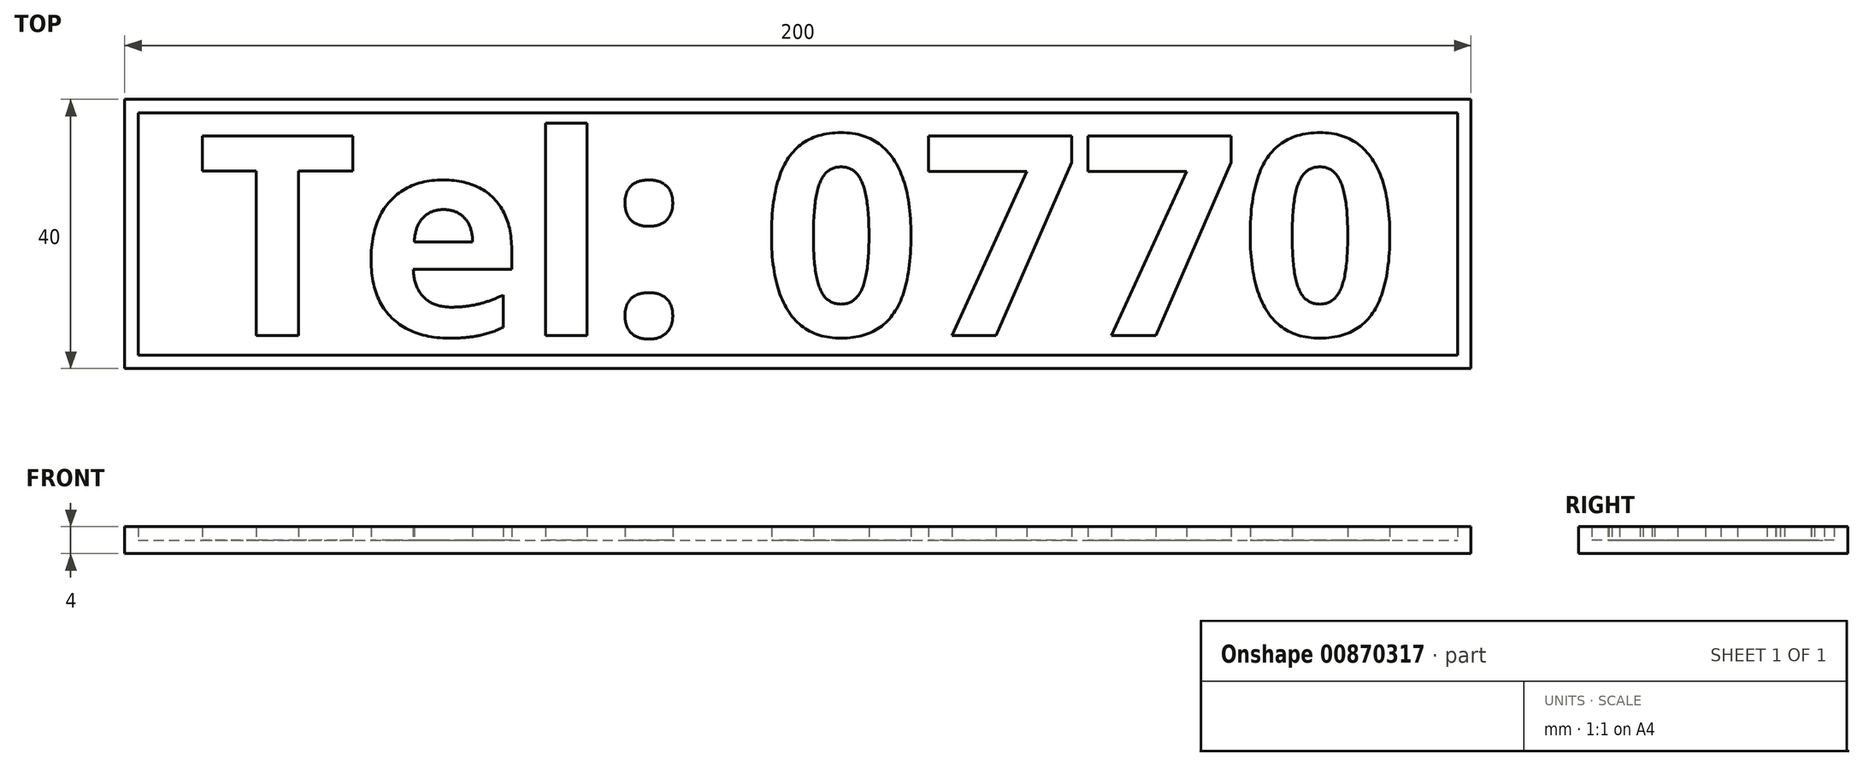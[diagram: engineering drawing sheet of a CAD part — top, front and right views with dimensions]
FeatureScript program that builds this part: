
annotation { "Feature Type Name" : "Feature", "Feature Type Description" : "" }
export const myFeature = defineFeature(function(context is Context, id is Id, definition is map)
    precondition{}
    {
        {
            var Q0;
            Q0=qCreatedBy(makeId("Top.planeOp"),FACE);
            var sketch = newSketch(context, id + "F0", { "sketchPlane" : qUnion([Q0])});
            skLineSegment(sketch, "E0.bottom", {"start": v(-100, 20) * mm, "end": v(100, 20) * mm});
            skLineSegment(sketch, "E0.top", {"start": v(-100, -20) * mm, "end": v(100, -20) * mm});
            skLineSegment(sketch, "E0.left", {"start": v(-100, 20) * mm, "end": v(-100, -20) * mm});
            skLineSegment(sketch, "E0.right", {"start": v(100, 20) * mm, "end": v(100, -20) * mm});
            skPoint(sketch, "E0.middle", {"position": v(0, 0) * mm});
            skLineSegment(sketch, "E1.bottom", {"start": v(-98, 18) * mm, "end": v(98, 18) * mm});
            skLineSegment(sketch, "E1.top", {"start": v(-98, -18) * mm, "end": v(98, -18) * mm});
            skLineSegment(sketch, "E1.left", {"start": v(-98, 18) * mm, "end": v(-98, -18) * mm});
            skLineSegment(sketch, "E1.right", {"start": v(98, 18) * mm, "end": v(98, -18) * mm});
            skSolve(sketch);
        }
        {
            var Q0;
            Q0=makeQuery(id+"F0.imprint","IMPRINT",FACE,{"disambiguationData":[TD([[makeQuery(id+"F0.imprint","IMPRINT",EDGE,{"derivedFrom":sQuery(id+"F0.wireOp",EDGE,"E1.bottom")}),-1.0]])]});
            extrude(context, id + "F1", {"entities" : qUnion([Q0]), "depth" : 2 * mm, "offsetDistance" : 25 * mm});
        }
        {
            var Q0;
            Q0=makeQuery(id+"F0.imprint","IMPRINT",FACE,{"disambiguationData":[TD([[makeQuery(id+"F0.imprint","IMPRINT",EDGE,{"derivedFrom":sQuery(id+"F0.wireOp",EDGE,"E0.bottom")}),-1.0]])]});
            extrude(context, id + "F2", {"entities" : qUnion([Q0]), "operationType" : NewBodyOperationType.ADD, "depth" : 4 * mm, "offsetDistance" : 25 * mm});
        }
        {
            var Q0;
            Q0=makeQuery(id+"F1.opExtrude","CAP_FACE",FACE,{"disambiguationData":[OSD([sQuery(id+"F0.wireOp",EDGE,"E1.bottom"),sQuery(id+"F0.wireOp",EDGE,"E1.top"),sQuery(id+"F0.wireOp",EDGE,"E1.left"),sQuery(id+"F0.wireOp",EDGE,"E1.right")])],"isStart":false});
            var sketch = newSketch(context, id + "F3", { "sketchPlane" : qUnion([Q0])});
            skText(sketch, "E2", { "text": "Tel: 0770", "fontName": "OpenSans-Bold.ttf"});
            const initialGuessF3  = {"E2": [-0.08933, -0.01507, 1, 0, 0.02991]};
            skSetInitialGuess(sketch, initialGuessF3);
            skSolve(sketch);
        }
        {
            var Q0;
            Q0 = qSketchRegion(id + "F3", true);
            extrude(context, id + "F4", {"entities" : qUnion([Q0]), "operationType" : NewBodyOperationType.ADD, "depth" : 2 * mm, "offsetDistance" : 25 * mm});
        }
    });
